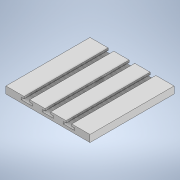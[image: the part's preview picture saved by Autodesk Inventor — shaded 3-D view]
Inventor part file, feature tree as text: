
AUTODESK INVENTOR PART (.ipt)
format: ipt  version: 2022 (Build 260153000, 153)  size: 137,728 bytes
history: native  units: in
note: dims shown in document units (in); Inventor stores cm internally (conversion verified against a paired STEP export)
features: extrude x1, sketch x1
ambient origin geometry x8: Origin, YZ Plane, XZ Plane, XY Plane, X Axis, Y Axis, Z Axis, Center Point
bodies: Solid1 (feature_tree)
feature tree (2):
  extrude  "Extrusion1"  Depth=23.622in
  sketch  "Sketch1"  dims[d0=11.811in d1=23.622in d2=1.9685in d3=1.9685in d4=0.7874in d5=0.7874in d6=0.7874in d7=0.7874in d8=1.1811in d9=0.5906in d10=0.5906in d11=1.1811in d12=2.9528in d13=2.9528in d14=0.5906in d15=4.3226in d16=5.6228in d17=4.3226in d18=5.8217in d19=23.622in d20=0.0in]
